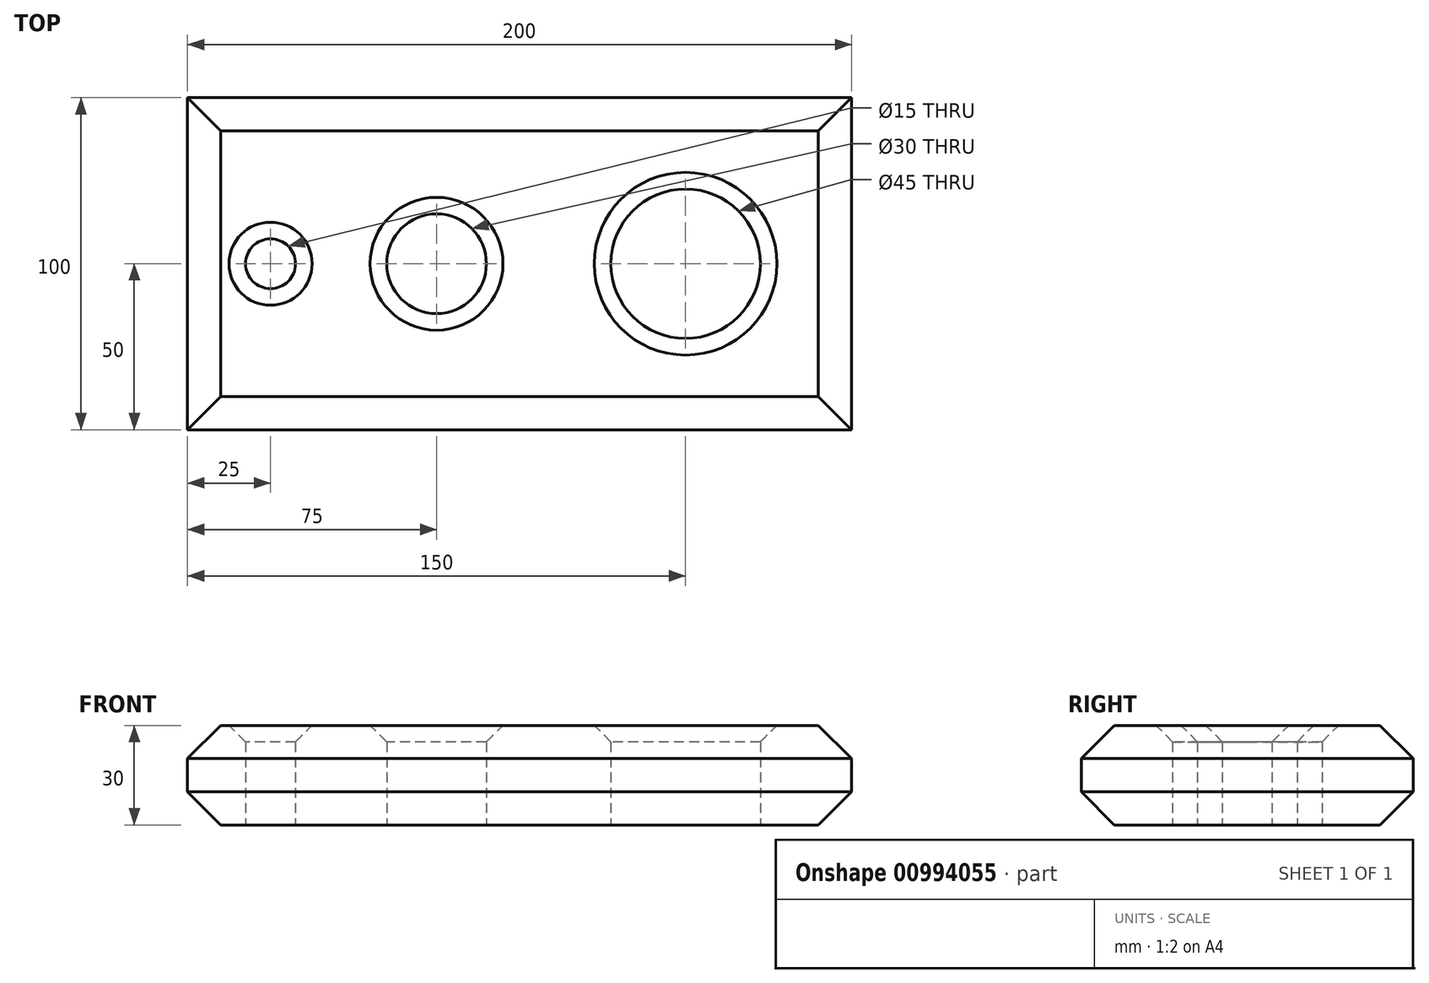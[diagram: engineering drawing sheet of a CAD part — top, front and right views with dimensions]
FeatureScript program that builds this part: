
annotation { "Feature Type Name" : "Feature", "Feature Type Description" : "" }
export const myFeature = defineFeature(function(context is Context, id is Id, definition is map)
    precondition{}
    {
        {
            var Q0;
            Q0=qCreatedBy(makeId("Top.planeOp"),FACE);
            var sketch = newSketch(context, id + "F0", { "sketchPlane" : qUnion([Q0])});
            skLineSegment(sketch, "E0.bottom", {"start": v(-100, 50) * mm, "end": v(100, 50) * mm});
            skLineSegment(sketch, "E0.top", {"start": v(-100, -50) * mm, "end": v(100, -50) * mm});
            skLineSegment(sketch, "E0.left", {"start": v(-100, 50) * mm, "end": v(-100, -50) * mm});
            skLineSegment(sketch, "E0.right", {"start": v(100, 50) * mm, "end": v(100, -50) * mm});
            skPoint(sketch, "E0.middle", {"position": v(0, 0) * mm});
            skLineSegment(sketch, "E1", {"start": v(-75, 60.7) * mm, "end": v(-75, -75.73) * mm, "construction": true});
            skLineSegment(sketch, "E2", {"start": v(-25, 61.1) * mm, "end": v(-25, -73.02) * mm, "construction": true});
            skLineSegment(sketch, "E3", {"start": v(50, 59.93) * mm, "end": v(50, -69.92) * mm, "construction": true});
            skLineSegment(sketch, "E4", {"start": v(-136.36, 0) * mm, "end": v(118.3, 0) * mm, "construction": true});
            skCircle(sketch, "E5", {"center": v(-75, 0) * mm, "radius": 7.5 * mm});
            skCircle(sketch, "E6", {"center": v(-25, 0) * mm, "radius": 15 * mm});
            skCircle(sketch, "E7", {"center": v(50, 0) * mm, "radius": 22.5 * mm});
            skSolve(sketch);
        }
        {
            var Q0;
            Q0=makeQuery(id+"F0.imprint","IMPRINT",FACE,{"disambiguationData":[TD([[makeQuery(id+"F0.imprint","IMPRINT",EDGE,{"derivedFrom":sQuery(id+"F0.wireOp",EDGE,"E0.bottom")}),-1.0]])]});
            extrude(context, id + "F1", {"entities" : qUnion([Q0]), "depth" : 30 * mm, "offsetDistance" : 25 * mm});
        }
        {
            var Q0;
            Q0=makeQuery(id+"F1.opExtrude","CAP_EDGE",EDGE,{"disambiguationData":[OSD([sQuery(id+"F0.wireOp",EDGE,"E5")])],"isStart":false});
            var Q1;
            Q1=makeQuery(id+"F1.opExtrude","CAP_EDGE",EDGE,{"disambiguationData":[OSD([sQuery(id+"F0.wireOp",EDGE,"E6")])],"isStart":false});
            var Q2;
            Q2=makeQuery(id+"F1.opExtrude","CAP_EDGE",EDGE,{"disambiguationData":[OSD([sQuery(id+"F0.wireOp",EDGE,"E7")])],"isStart":false});
            chamfer(context, id + "F2", {"entities" : qUnion([Q0, Q1, Q2]), "chamferType" : ChamferType.OFFSET_ANGLE, "width" : 5 * mm, "oppositeDirection" : false, "angle" : 45 * degree, "tangentPropagation" : true});
        }
        {
            var Q0;
            Q0=makeQuery(id+"F1.opExtrude","CAP_EDGE",EDGE,{"disambiguationData":[OSD([sQuery(id+"F0.wireOp",EDGE,"E0.left")])],"isStart":false});
            var Q1;
            Q1=makeQuery(id+"F1.opExtrude","CAP_EDGE",EDGE,{"disambiguationData":[OSD([sQuery(id+"F0.wireOp",EDGE,"E0.bottom")])],"isStart":false});
            var Q2;
            Q2=makeQuery(id+"F1.opExtrude","CAP_EDGE",EDGE,{"disambiguationData":[OSD([sQuery(id+"F0.wireOp",EDGE,"E0.right")])],"isStart":false});
            var Q3;
            Q3=makeQuery(id+"F1.opExtrude","CAP_EDGE",EDGE,{"disambiguationData":[OSD([sQuery(id+"F0.wireOp",EDGE,"E0.top")])],"isStart":false});
            var Q4;
            Q4=makeQuery(id+"F1.opExtrude","CAP_EDGE",EDGE,{"disambiguationData":[OSD([sQuery(id+"F0.wireOp",EDGE,"E0.top")])],"isStart":true});
            var Q5;
            Q5=makeQuery(id+"F1.opExtrude","CAP_EDGE",EDGE,{"disambiguationData":[OSD([sQuery(id+"F0.wireOp",EDGE,"E0.left")])],"isStart":true});
            var Q6;
            Q6=makeQuery(id+"F1.opExtrude","CAP_EDGE",EDGE,{"disambiguationData":[OSD([sQuery(id+"F0.wireOp",EDGE,"E0.bottom")])],"isStart":true});
            var Q7;
            Q7=makeQuery(id+"F1.opExtrude","CAP_EDGE",EDGE,{"disambiguationData":[OSD([sQuery(id+"F0.wireOp",EDGE,"E0.right")])],"isStart":true});
            chamfer(context, id + "F3", {"entities" : qUnion([Q0, Q1, Q2, Q3, Q4, Q5, Q6, Q7]), "chamferType" : ChamferType.OFFSET_ANGLE, "width" : 10 * mm, "oppositeDirection" : false, "angle" : 45 * degree, "tangentPropagation" : true});
        }
    });
